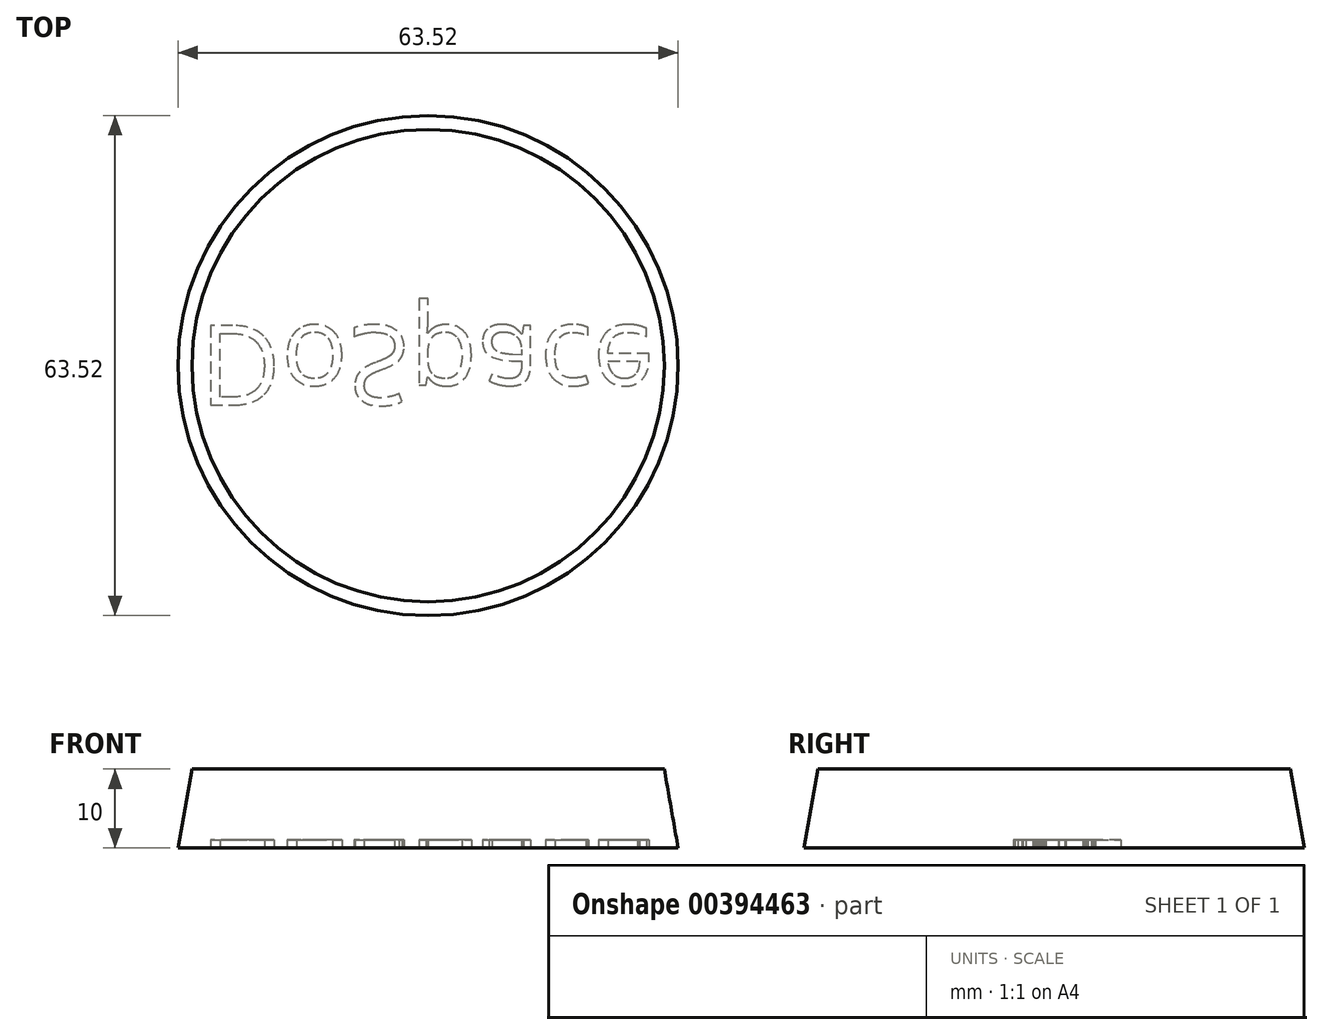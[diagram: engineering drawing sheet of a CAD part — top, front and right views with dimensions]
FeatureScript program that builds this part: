
annotation { "Feature Type Name" : "Feature", "Feature Type Description" : "" }
export const myFeature = defineFeature(function(context is Context, id is Id, definition is map)
    precondition{}
    {
        {
            var Q0;
            Q0=qCreatedBy(makeId("Top.planeOp"),FACE);
            var sketch = newSketch(context, id + "F0", { "sketchPlane" : qUnion([Q0])});
            skCircle(sketch, "E0", {"center": v(0, 0) * mm, "radius": 30 * mm});
            skSolve(sketch);
        }
        {
            var Q0;
            Q0=makeQuery(id+"F0.imprint","IMPRINT",FACE,{"disambiguationData":[TD([[makeQuery(id+"F0.imprint","IMPRINT",EDGE,{"derivedFrom":sQuery(id+"F0.wireOp",EDGE,"E0")}),1.0]])]});
            extrude(context, id + "F1", {"entities" : qUnion([Q0]), "oppositeDirection" : true, "depth" : 10 * mm, "hasDraft" : true, "draftAngle" : 10 * degree});
        }
        {
            var Q0;
            Q0=makeQuery(id+"F1.opExtrude","CAP_FACE",FACE,{"disambiguationData":[OSD([sQuery(id+"F0.wireOp",EDGE,"E0")])],"isStart":false});
            var sketch = newSketch(context, id + "F2", { "sketchPlane" : qUnion([Q0])});
            skText(sketch, "E1", { "text": "DoSpace", "fontName": "OpenSans-Regular.ttf"});
            const initialGuessF2  = {"E1": [-0.029, -0.0051, 1, 0, 0.01018]};
            skSetInitialGuess(sketch, initialGuessF2);
            skSolve(sketch);
        }
        {
            var Q0;
            Q0=qSketchRegion(id+"F2",true);
            extrude(context, id + "F3", {"entities" : qUnion([Q0]), "operationType" : NewBodyOperationType.REMOVE, "oppositeDirection" : true, "depth" : 1 * mm});
        }
    });
